# Revit family: Hager-VECTOR-Surface_mounted-IP65-With_Cover-With_DIN-NoHosted-SE-en
name_source: partatom
category: Electrical Equipment
units: mm (PartAtom-declared; Revit-internal decimal feet)

## family parameters
Always vertical = Yes
Cut with Voids When Loaded = No
Maintain Annotation Orientation = No
Panel Configuration = Two Columns, Circuits Across
Part Type = Panelboard
Room Calculation Point = No
Round Connector Dimension = Use Diameter
Shared = No
Work Plane-Based = Yes

## types (20) — shared parameters
Code hager = ADD-EC000214_EU
Default Elevation = 1200 mm
EF000003 - Mounting method = Surface mounted
EF000007 - Colour = Grey
EF000024 - UV resistant = No
EF000116 - RAL-number = 7035
EF000118 - With mounting plate = No
EF001062 - EMC-version = No
EF001088 - Extension possible = Yes
EF001134 - DIN-rail = Yes
EF004462 - Type of closure = Other
EF005474 - Degree of protection (IP) = IP65
EF006306 - With lock = No
EF015941 - Signal passing door = Yes
ETIM class code = EC000214
ETIM class name = Small distribution board
HG000001-Number of columns = 1
HG000002-With door or cover = Yes
HG000003-Range = VECTOR
HG000005-Thickness = 2 mm  [stored 0.00656168 ft]
HG000006-Flush mounted = No
HG000009-Double swing door = No
HG000010-Asymmetric doors = No
HG000011-Empty rows from bottom = No
HG000012-Door swing angle = 90.00°
HG000013-Door on the left = No
HG000014-Door on the right = Yes
HG000015-Clearance visibility = Yes
HG000016-Door 3D visibility = Yes
HG000017-Distance between poles = 18 mm  [stored 0.0590551 ft]
HG000060-RAL-number = 7035
HG000099-Onfly Template ID = 507532
Manufacturer = Hager
Name BIM&CO = Electricity
Name hager = ADD_Enclosures_EC000214
Reference = Template-Enclosure_EU-EC000214
Uniformat = Low Tension Service & Dist.
Uniformat code = D501001
zero-valued in all types: EF000218 - Built-in depth, EF000332 - Built-in height, EF000846 - Built-in width, EF001131 - Inner depth, HG000007-Number of empty columns, HG000008-Number of empty rows

## per-type parameters (varying)
| type | BC_METADATA | EF000008 - Width | EF000040 - Height | EF000049 - Depth | EF000266 - Number of rows | EF002950 - Width in number of modular spacings | EF006244 - Transparent cover/door | EF009212 - Cover model | EF015776 - Earthing terminal block | EF015777 - Neutral terminal block | HG000004-Manufacturer reference | HGEF000266-Number of rows | HGEF002950-Width in number of modular spacings |
| VECTOR-Surface_mounted_W111_H175_D93_3_Modular_Spacing-VE103PN | {"ObjectGuid":"8585df22-46b9-4029-a56c-8c9545ce093a","ModelGuid":"917c4e0b-dbe5-40e2-9642-e7636be6e4c6","VariantGuid":"dceed055-01a0-40e0-809f-1cc6755ae138","Revision":"#3","VariantName":"VECTOR-Surface_mounted_W111_H175_D93_3_Modular_Spacing-VE103PN"} | 111 mm | 175 mm  [stored 0.574147 ft] | 93 mm  [stored 0.305118 ft] | 1 | 3 | Yes | With notch | No | No | VE103PN | 1 | 3 |
| VECTOR-Surface_mounted_W111_H175_D93_3_Modular_Spacing-VE103S | {"ObjectGuid":"8585df22-46b9-4029-a56c-8c9545ce093a","ModelGuid":"917c4e0b-dbe5-40e2-9642-e7636be6e4c6","VariantGuid":"3da4f0a7-ab85-456a-a781-72b0088e1fe4","Revision":"#3","VariantName":"VECTOR-Surface_mounted_W111_H175_D93_3_Modular_Spacing-VE103S"} | 111 mm | 175 mm  [stored 0.574147 ft] | 93 mm  [stored 0.305118 ft] | 1 | 3 | Yes | Closed | Yes | Yes | VE103S | 1 | 3 |
| VECTOR-Surface_mounted_W165_H190_D113_6_Modular_Spacing-VE106PN | {"ObjectGuid":"8585df22-46b9-4029-a56c-8c9545ce093a","ModelGuid":"917c4e0b-dbe5-40e2-9642-e7636be6e4c6","VariantGuid":"9a8f9e52-c501-4968-8197-d81011ca3501","Revision":"#3","VariantName":"VECTOR-Surface_mounted_W165_H190_D113_6_Modular_Spacing-VE106PN"} | 165 mm | 190 mm | 113 mm | 1 | 6 | Yes | Closed | No | No | VE106PN | 1 | 6 |
| VECTOR-Surface_mounted_W165_H190_D113_6_Modular_Spacing-VE106S | {"ObjectGuid":"8585df22-46b9-4029-a56c-8c9545ce093a","ModelGuid":"917c4e0b-dbe5-40e2-9642-e7636be6e4c6","VariantGuid":"021de0e3-b4cb-44d2-aafa-1aeb9ac8b5d1","Revision":"#3","VariantName":"VECTOR-Surface_mounted_W165_H190_D113_6_Modular_Spacing-VE106S"} | 165 mm | 190 mm | 113 mm | 1 | 6 | Yes | Closed | Yes | Yes | VE106S | 1 | 6 |
| VECTOR-Surface_mounted_W237_H210_D114_10_Modular_Spacing-VE110PN | {"ObjectGuid":"8585df22-46b9-4029-a56c-8c9545ce093a","ModelGuid":"917c4e0b-dbe5-40e2-9642-e7636be6e4c6","VariantGuid":"7d1317c1-3255-442e-811d-ce4febf7792a","Revision":"#3","VariantName":"VECTOR-Surface_mounted_W237_H210_D114_10_Modular_Spacing-VE110PN"} | 237 mm | 210 mm | 114 mm | 1 | 10 | Yes | Closed | No | No | VE110PN | 1 | 10 |
| VECTOR-Surface_mounted_W237_H210_D114_10_Modular_Spacing-VE110S | {"ObjectGuid":"8585df22-46b9-4029-a56c-8c9545ce093a","ModelGuid":"917c4e0b-dbe5-40e2-9642-e7636be6e4c6","VariantGuid":"86688245-9f57-4885-a1af-70940fbfb577","Revision":"#3","VariantName":"VECTOR-Surface_mounted_W237_H210_D114_10_Modular_Spacing-VE110S"} | 237 mm | 210 mm | 114 mm | 1 | 10 | Yes | Closed | Yes | Yes | VE110S | 1 | 10 |
| VECTOR-Surface_mounted_W310_H302_D151_12_Modular_Spacing-VE112PN | {"ObjectGuid":"8585df22-46b9-4029-a56c-8c9545ce093a","ModelGuid":"917c4e0b-dbe5-40e2-9642-e7636be6e4c6","VariantGuid":"0a6638ae-4f1e-4f4a-9623-43977fa7400f","Revision":"#3","VariantName":"VECTOR-Surface_mounted_W310_H302_D151_12_Modular_Spacing-VE112PN"} | 310 mm | 302 mm | 151 mm | 1 | 12 | Yes | Closed | No | No | VE112PN | 1 | 12 |
| VECTOR-Surface_mounted_W310_H302_D151_12_Modular_Spacing-VE112S | {"ObjectGuid":"8585df22-46b9-4029-a56c-8c9545ce093a","ModelGuid":"917c4e0b-dbe5-40e2-9642-e7636be6e4c6","VariantGuid":"f5b09366-b00f-4011-a6a2-6258572b6126","Revision":"#3","VariantName":"VECTOR-Surface_mounted_W310_H302_D151_12_Modular_Spacing-VE112S"} | 310 mm | 302 mm | 151 mm | 1 | 12 | No | Closed | Yes | Yes | VE112S | 1 | 12 |
| VECTOR-Surface_mounted_W418_H302_D151_18_Modular_Spacing-VE118PN | {"ObjectGuid":"8585df22-46b9-4029-a56c-8c9545ce093a","ModelGuid":"917c4e0b-dbe5-40e2-9642-e7636be6e4c6","VariantGuid":"a2d36401-f512-47e5-8ccf-746d4b91cff7","Revision":"#3","VariantName":"VECTOR-Surface_mounted_W418_H302_D151_18_Modular_Spacing-VE118PN"} | 418 mm | 302 mm | 151 mm | 1 | 18 | Yes | Closed | No | No | VE118PN | 1 | 18 |
| VECTOR-Surface_mounted_W418_H302_D151_18_Modular_Spacing-VE118S | {"ObjectGuid":"8585df22-46b9-4029-a56c-8c9545ce093a","ModelGuid":"917c4e0b-dbe5-40e2-9642-e7636be6e4c6","VariantGuid":"6a37b257-360f-43e6-ace8-b2a14b084196","Revision":"#3","VariantName":"VECTOR-Surface_mounted_W418_H302_D151_18_Modular_Spacing-VE118S"} | 418 mm | 302 mm | 151 mm | 1 | 18 | No | Closed | Yes | Yes | VE118S | 1 | 18 |
| VECTOR-Surface_mounted_W310_H427_D151_12_Modular_Spacing-VE212PN | {"ObjectGuid":"8585df22-46b9-4029-a56c-8c9545ce093a","ModelGuid":"917c4e0b-dbe5-40e2-9642-e7636be6e4c6","VariantGuid":"7154170c-1f55-4b2a-8155-f35b4c7a3942","Revision":"#3","VariantName":"VECTOR-Surface_mounted_W310_H427_D151_12_Modular_Spacing-VE212PN"} | 310 mm | 427 mm | 151 mm | 2 | 12 | Yes | Closed | No | No | VE212PN | 2 | 12 |
| VECTOR-Surface_mounted_W310_H427_D151_12_Modular_Spacing-VE212S | {"ObjectGuid":"8585df22-46b9-4029-a56c-8c9545ce093a","ModelGuid":"917c4e0b-dbe5-40e2-9642-e7636be6e4c6","VariantGuid":"f8eeaf46-f133-4f38-8d6d-92988228d15c","Revision":"#3","VariantName":"VECTOR-Surface_mounted_W310_H427_D151_12_Modular_Spacing-VE212S"} | 310 mm | 427 mm | 151 mm | 2 | 12 | No | Closed | Yes | Yes | VE212S | 2 | 12 |
| VECTOR-Surface_mounted_W418_H452_D151_18_Modular_Spacing-VE218PN | {"ObjectGuid":"8585df22-46b9-4029-a56c-8c9545ce093a","ModelGuid":"917c4e0b-dbe5-40e2-9642-e7636be6e4c6","VariantGuid":"f3856140-5f26-4806-9296-c0d92ec9952e","Revision":"#3","VariantName":"VECTOR-Surface_mounted_W418_H452_D151_18_Modular_Spacing-VE218PN"} | 418 mm | 452 mm | 151 mm | 2 | 18 | Yes | Closed | No | No | VE218PN | 2 | 18 |
| VECTOR-Surface_mounted_W418_H452_D151_18_Modular_Spacing-VE218S | {"ObjectGuid":"8585df22-46b9-4029-a56c-8c9545ce093a","ModelGuid":"917c4e0b-dbe5-40e2-9642-e7636be6e4c6","VariantGuid":"c66a5f04-c84e-419c-a4ae-a735c563f0d7","Revision":"#3","VariantName":"VECTOR-Surface_mounted_W418_H452_D151_18_Modular_Spacing-VE218S"} | 418 mm | 452 mm | 151 mm | 2 | 18 | No | Closed | Yes | Yes | VE218S | 2 | 18 |
| VECTOR-Surface_mounted_W310_H552_D151_12_Modular_Spacing-VE312PN | {"ObjectGuid":"8585df22-46b9-4029-a56c-8c9545ce093a","ModelGuid":"917c4e0b-dbe5-40e2-9642-e7636be6e4c6","VariantGuid":"6981c1fa-d4cb-404b-832b-0b22869bcef5","Revision":"#3","VariantName":"VECTOR-Surface_mounted_W310_H552_D151_12_Modular_Spacing-VE312PN"} | 310 mm | 552 mm | 151 mm | 3 | 12 | Yes | Closed | No | No | VE312PN | 3 | 12 |
| VECTOR-Surface_mounted_W310_H552_D151_12_Modular_Spacing-VE312S | {"ObjectGuid":"8585df22-46b9-4029-a56c-8c9545ce093a","ModelGuid":"917c4e0b-dbe5-40e2-9642-e7636be6e4c6","VariantGuid":"8db7e214-e04c-4fbe-bba5-c6cfb8eb75fc","Revision":"#3","VariantName":"VECTOR-Surface_mounted_W310_H552_D151_12_Modular_Spacing-VE312S"} | 310 mm | 552 mm | 151 mm | 3 | 12 | No | Closed | Yes | Yes | VE312S | 3 | 12 |
| VECTOR-Surface_mounted_W418_H602_D151_18_Modular_Spacing-VE318PN | {"ObjectGuid":"8585df22-46b9-4029-a56c-8c9545ce093a","ModelGuid":"917c4e0b-dbe5-40e2-9642-e7636be6e4c6","VariantGuid":"6b750252-c4d3-42fa-8166-b02792a9c542","Revision":"#3","VariantName":"VECTOR-Surface_mounted_W418_H602_D151_18_Modular_Spacing-VE318PN"} | 418 mm | 602 mm | 151 mm | 3 | 18 | Yes | Closed | No | No | VE318PN | 3 | 18 |
| VECTOR-Surface_mounted_W418_H602_D151_18_Modular_Spacing-VE318S | {"ObjectGuid":"8585df22-46b9-4029-a56c-8c9545ce093a","ModelGuid":"917c4e0b-dbe5-40e2-9642-e7636be6e4c6","VariantGuid":"f8872fc8-e466-4496-9bed-d8bb85af5d52","Revision":"#3","VariantName":"VECTOR-Surface_mounted_W418_H602_D151_18_Modular_Spacing-VE318S"} | 418 mm | 602 mm | 151 mm | 3 | 18 | No | Closed | Yes | Yes | VE318S | 3 | 18 |
| VECTOR-Surface_mounted_W310_H677_D151_12_Modular_Spacing-VE412PN | {"ObjectGuid":"8585df22-46b9-4029-a56c-8c9545ce093a","ModelGuid":"917c4e0b-dbe5-40e2-9642-e7636be6e4c6","VariantGuid":"4dc323a7-6a48-401f-9820-fe78de50fd4e","Revision":"#3","VariantName":"VECTOR-Surface_mounted_W310_H677_D151_12_Modular_Spacing-VE412PN"} | 310 mm | 677 mm | 151 mm | 4 | 12 | Yes | Closed | No | No | VE412PN | 4 | 12 |
| VECTOR-Surface_mounted_W310_H677_D151_12_Modular_Spacing-VE412S | {"ObjectGuid":"8585df22-46b9-4029-a56c-8c9545ce093a","ModelGuid":"917c4e0b-dbe5-40e2-9642-e7636be6e4c6","VariantGuid":"02dcc49b-23ec-45c8-a3e5-50699862c434","Revision":"#3","VariantName":"VECTOR-Surface_mounted_W310_H677_D151_12_Modular_Spacing-VE412S"} | 310 mm | 677 mm | 151 mm | 4 | 12 | No | Closed | Yes | Yes | VE412S | 4 | 12 |

note: [stored X ft] marks values corroborated as IEEE doubles in the binary element streams (Revit-internal decimal feet)

## geometry (parser evidence)
native form markers: Sweep x13
no freeform markers — native parametric forms only
